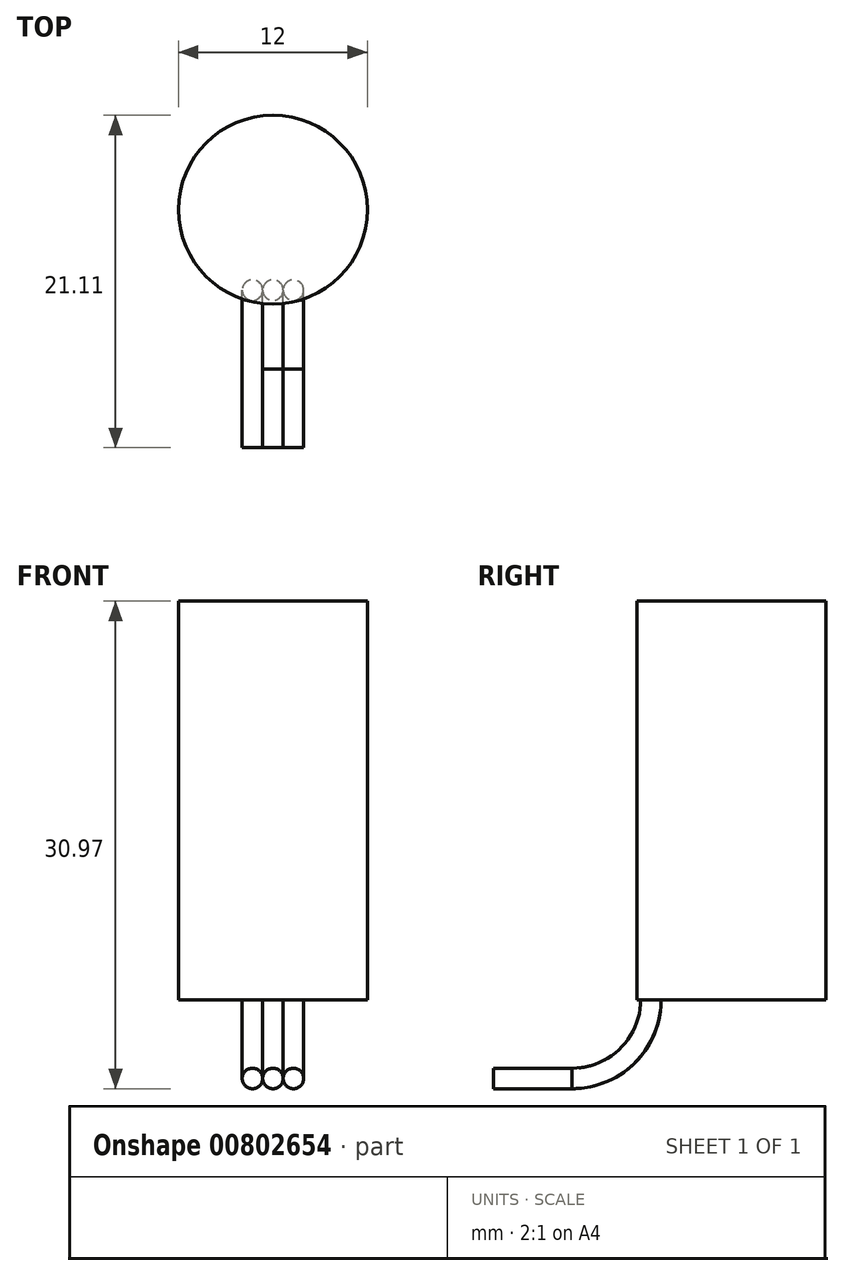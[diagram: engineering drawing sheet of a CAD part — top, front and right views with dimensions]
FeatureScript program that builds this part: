
annotation { "Feature Type Name" : "Feature", "Feature Type Description" : "" }
export const myFeature = defineFeature(function(context is Context, id is Id, definition is map)
    precondition{}
    {
        {
            var Q0;
            Q0=qCreatedBy(makeId("Top.planeOp"),FACE);
            var sketch = newSketch(context, id + "F0", { "sketchPlane" : qUnion([Q0])});
            skCircle(sketch, "E0", {"center": v(0, 0) * mm, "radius": 6 * mm});
            skSolve(sketch);
        }
        {
            var Q0;
            Q0 = qSketchRegion(id + "F0", true);
            extrude(context, id + "F1", {"entities" : qUnion([Q0]), "depth" : 25.32 * mm, "offsetDistance" : 25.4 * mm});
        }
        {
            var Q0;
            Q0=makeQuery(id+"F1.opExtrude","CAP_FACE",FACE,{"disambiguationData":[OSD([sQuery(id+"F0.wireOp",EDGE,"E0")])],"isStart":true});
            var sketch = newSketch(context, id + "F2", { "sketchPlane" : qUnion([Q0])});
            skLineSegment(sketch, "E1", {"start": v(0, 0) * mm, "end": v(0, 21.72) * mm, "construction": true});
            skLineSegment(sketch, "E2.bottom", {"start": v(-3.15, 5.1) * mm, "end": v(3.15, 5.1) * mm, "construction": true});
            skLineSegment(sketch, "E2.top", {"start": v(-3.15, -5.1) * mm, "end": v(3.15, -5.1) * mm, "construction": true});
            skLineSegment(sketch, "E2.left", {"start": v(-3.15, 5.1) * mm, "end": v(-3.15, -5.1) * mm, "construction": true});
            skLineSegment(sketch, "E2.right", {"start": v(3.15, 5.1) * mm, "end": v(3.15, -5.1) * mm, "construction": true});
            skPoint(sketch, "E2.middle", {"position": v(0, 0) * mm});
            skCircle(sketch, "E3", {"center": v(0, 5.1) * mm, "radius": 0.65 * mm});
            skLineSegment(sketch, "E4", {"start": v(-0.65, 5.1) * mm, "end": v(-1.3, 5.1) * mm, "construction": true});
            skCircle(sketch, "E5", {"center": v(-1.3, 5.1) * mm, "radius": 0.65 * mm});
            skLineSegment(sketch, "E6", {"start": v(0.65, 5.1) * mm, "end": v(1.3, 5.1) * mm, "construction": true});
            skCircle(sketch, "E7", {"center": v(1.3, 5.1) * mm, "radius": 0.65 * mm});
            skLineSegment(sketch, "E8", {"start": v(0, 5.1) * mm, "end": v(0, 10.1) * mm, "construction": true});
            skLineSegment(sketch, "E9", {"start": v(0, 10.1) * mm, "end": v(3.16, 10.1) * mm, "construction": true});
            skSolve(sketch);
        }
        {
            var Q0;
            {var subQ0=sQuery(id+"F2.wireOp",EDGE,"E3");var subQ1=makeQuery(id+"F2.imprint","INTERSECT",VERTEX,{"derivedFrom":[subQ0,sQuery(id+"F2.wireOp",EDGE,"E5")]});Q0=makeQuery(id+"F2.imprint","IMPRINT",FACE,{"disambiguationData":[TD([[makeQuery(id+"F2.imprint","IMPRINT",EDGE,{"disambiguationData":[TD([[subQ1,1.0]])],"derivedFrom":subQ0}),1.0]])]});}
            var Q1;
            Q1=makeQuery(id+"F2.imprint","IMPRINT",FACE,{"disambiguationData":[TD([[makeQuery(id+"F2.imprint","IMPRINT",EDGE,{"derivedFrom":sQuery(id+"F2.wireOp",EDGE,"E5")}),1.0]])]});
            var Q2;
            Q2=makeQuery(id+"F2.imprint","IMPRINT",FACE,{"disambiguationData":[TD([[makeQuery(id+"F2.imprint","IMPRINT",EDGE,{"derivedFrom":sQuery(id+"F2.wireOp",EDGE,"E7")}),1.0]])]});
            var Q3;
            Q3=sQuery(id+"F2.wireOp",EDGE,"E9");
            revolve(context, id + "F3", {"surfaceOperationType" : NewSurfaceOperationType.NEW, "entities" : qUnion([Q0, Q1, Q2]), "axis" : qUnion([Q3]), "revolveType" : RevolveType.ONE_DIRECTION, "oppositeDirection" : true, "angle" : 90 * degree});
        }
        {
            var Q0;
            Q0=makeQuery(id+"F3.opRevolve","CAP_FACE",FACE,{"disambiguationData":[OSD([sQuery(id+"F2.wireOp",EDGE,"E5")])],"isStart":false});
            extrude(context, id + "F4", {"entities" : qUnion([Q0]), "operationType" : NewBodyOperationType.ADD, "depth" : 5 * mm, "offsetDistance" : 25.4 * mm});
        }
        {
            var Q0;
            Q0=makeQuery(id+"F3.opRevolve","CAP_FACE",FACE,{"disambiguationData":[OSD([sQuery(id+"F2.wireOp",EDGE,"E3")])],"isStart":false});
            extrude(context, id + "F5", {"entities" : qUnion([Q0]), "depth" : 5 * mm, "offsetDistance" : 25.4 * mm});
        }
        {
            var Q0;
            Q0=makeQuery(id+"F3.opRevolve","CAP_FACE",FACE,{"disambiguationData":[OSD([sQuery(id+"F2.wireOp",EDGE,"E7")])],"isStart":false});
            extrude(context, id + "F6", {"entities" : qUnion([Q0]), "depth" : 5 * mm, "offsetDistance" : 25.4 * mm});
        }
    });
